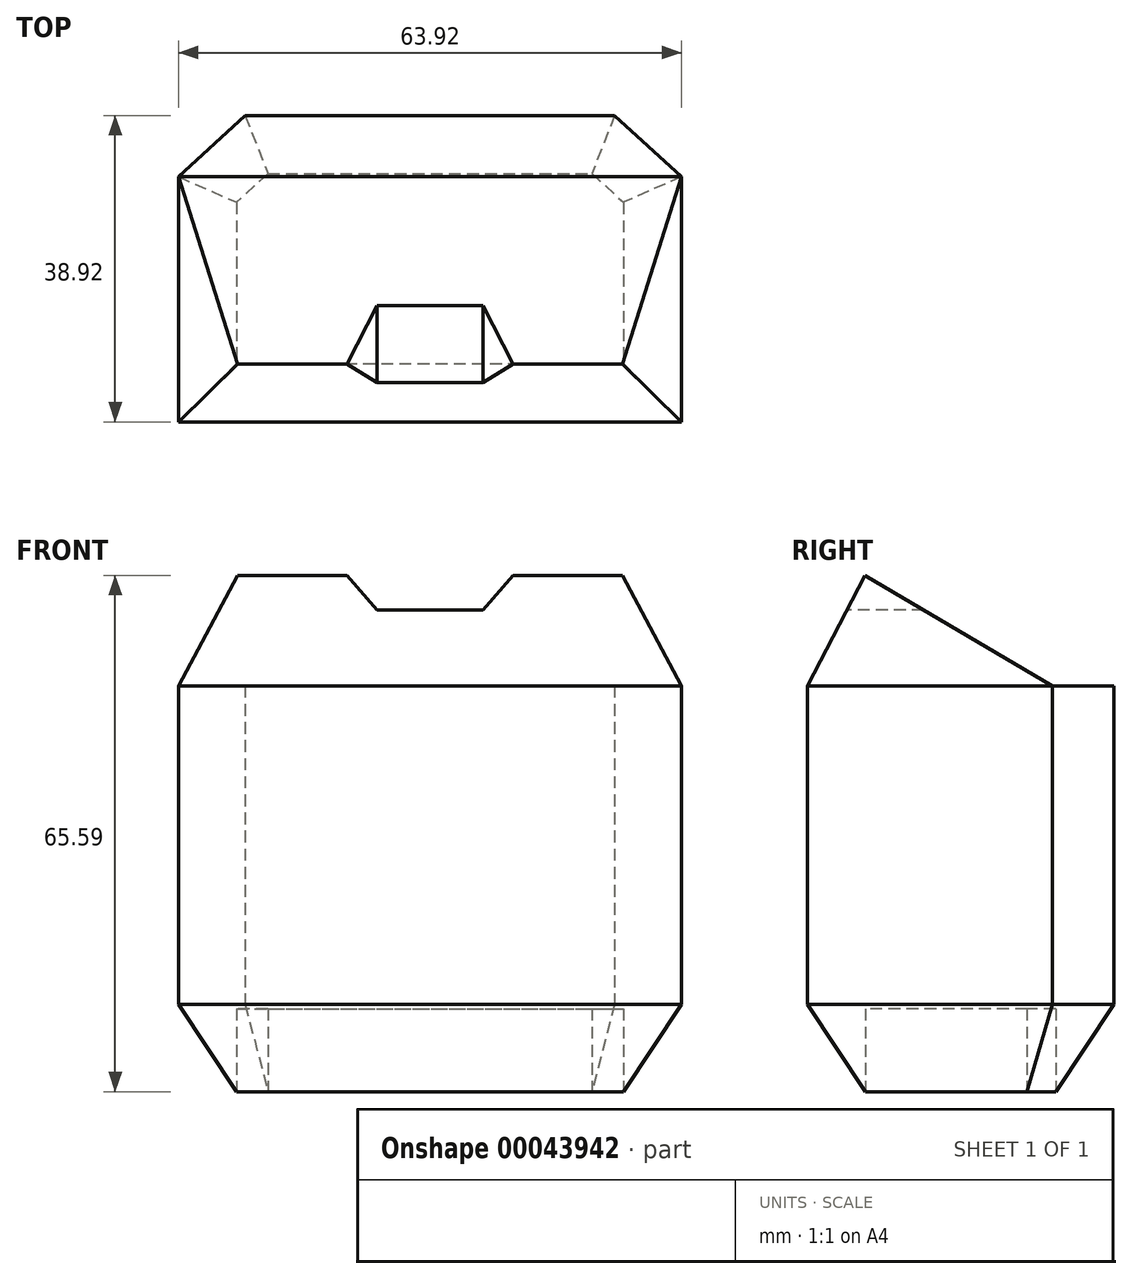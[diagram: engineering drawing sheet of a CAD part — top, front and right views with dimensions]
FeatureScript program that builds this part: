
annotation { "Feature Type Name" : "Feature", "Feature Type Description" : "" }
export const myFeature = defineFeature(function(context is Context, id is Id, definition is map)
    precondition{}
    {
        {
            var Q0;
            Q0=qCreatedBy(makeId("Top.planeOp"),FACE);
            var sketch = newSketch(context, id + "F0", { "sketchPlane" : qUnion([Q0])});
            skLineSegment(sketch, "E0", {"start": v(-23.46, 21.92) * mm, "end": v(23.46, 21.92) * mm});
            skLineSegment(sketch, "E1", {"start": v(23.46, 21.92) * mm, "end": v(31.96, 14.14) * mm});
            skLineSegment(sketch, "E2", {"start": v(31.96, 14.14) * mm, "end": v(31.96, -17) * mm});
            skLineSegment(sketch, "E3", {"start": v(31.96, -17) * mm, "end": v(0, -17) * mm});
            skLineSegment(sketch, "E4.MirrorCS", {"start": v(-31.96, 14.14) * mm, "end": v(-31.96, -17) * mm});
            skLineSegment(sketch, "E5.MirrorCS", {"start": v(-23.46, 21.92) * mm, "end": v(-31.96, 14.14) * mm});
            skLineSegment(sketch, "E6.MirrorCS", {"start": v(-31.96, -17) * mm, "end": v(0, -17) * mm});
            skLineSegment(sketch, "E7.0", {"start": v(-20.59, 14.54) * mm, "end": v(-24.57, 10.88) * mm});
            skLineSegment(sketch, "E7.1", {"start": v(-20.59, 14.54) * mm, "end": v(20.59, 14.54) * mm});
            skLineSegment(sketch, "E7.2", {"start": v(-24.57, -9.61) * mm, "end": v(0, -9.61) * mm});
            skLineSegment(sketch, "E7.3", {"start": v(24.57, -9.61) * mm, "end": v(0, -9.61) * mm});
            skLineSegment(sketch, "E7.4", {"start": v(24.57, 10.88) * mm, "end": v(24.57, -9.61) * mm});
            skLineSegment(sketch, "E7.5", {"start": v(-24.57, 10.88) * mm, "end": v(-24.57, -9.61) * mm});
            skLineSegment(sketch, "E7.6", {"start": v(20.59, 14.54) * mm, "end": v(24.57, 10.88) * mm});
            skSolve(sketch);
        }
        {
            var Q0;
            Q0=makeQuery(id+"F0.imprint","IMPRINT",FACE,{"disambiguationData":[TD([[makeQuery(id+"F0.imprint","IMPRINT",EDGE,{"derivedFrom":sQuery(id+"F0.wireOp",EDGE,"E7.0")}),1.0]])]});
            extrude(context, id + "F1", {"entities" : qUnion([Q0]), "depth" : 10.54 * mm});
        }
        {
            var Q0;
            Q0=makeQuery(id+"F1.opExtrude","SWEPT_BODY",BODY,{"disambiguationData":[OSD([sQuery(id+"F0.wireOp",EDGE,"E7.0"),sQuery(id+"F0.wireOp",EDGE,"E7.1"),sQuery(id+"F0.wireOp",EDGE,"E7.2"),sQuery(id+"F0.wireOp",EDGE,"E7.3"),sQuery(id+"F0.wireOp",EDGE,"E7.4"),sQuery(id+"F0.wireOp",EDGE,"E7.5"),sQuery(id+"F0.wireOp",EDGE,"E7.6")])]});
            var Q1;
            Q1=qCreatedBy(makeId("Top.planeOp"),FACE);
            transform(context, id + "F2", {"entities" : qUnion([Q0]), "transformType" : TransformType.TRANSLATION_DISTANCE, "transformDirection" : qUnion([Q1]), "distance" : 11.08 * mm, "oppositeDirection" : true, "makeCopy" : false});
        }
        {
            var Q0;
            Q0 = qSketchRegion(id + "F0", true);
            var Q1;
            Q1=makeQuery(id+"F0.imprint","IMPRINT",FACE,{"disambiguationData":[TD([[makeQuery(id+"F0.imprint","IMPRINT",EDGE,{"derivedFrom":sQuery(id+"F0.wireOp",EDGE,"E7.0")}),1.0]])]});
            extrude(context, id + "F3", {"entities" : qUnion([Q0, Q1]), "depth" : 40.48 * mm});
        }
        {
            var Q0;
            Q0=makeQuery(id+"F3.opExtrude","CAP_FACE",FACE,{"disambiguationData":[OSD([sQuery(id+"F0.wireOp",EDGE,"E0"),sQuery(id+"F0.wireOp",EDGE,"E1"),sQuery(id+"F0.wireOp",EDGE,"E2"),sQuery(id+"F0.wireOp",EDGE,"E3"),sQuery(id+"F0.wireOp",EDGE,"E4.MirrorCS"),sQuery(id+"F0.wireOp",EDGE,"E5.MirrorCS"),sQuery(id+"F0.wireOp",EDGE,"E6.MirrorCS")])],"isStart":true});
            var Q1;
            Q1=makeQuery(id+"F1.opExtrude","CAP_FACE",FACE,{"disambiguationData":[OSD([sQuery(id+"F0.wireOp",EDGE,"E7.0"),sQuery(id+"F0.wireOp",EDGE,"E7.1"),sQuery(id+"F0.wireOp",EDGE,"E7.2"),sQuery(id+"F0.wireOp",EDGE,"E7.3"),sQuery(id+"F0.wireOp",EDGE,"E7.4"),sQuery(id+"F0.wireOp",EDGE,"E7.5"),sQuery(id+"F0.wireOp",EDGE,"E7.6")])],"isStart":true});
            loft(context, id + "F4", {"sheetProfilesArray" : [{ "sheetProfileEntities" : qUnion([Q0]) }, { "sheetProfileEntities" : qUnion([Q1]) }]});
        }
        {
            var Q0;
            Q0=makeQuery(id+"F3.opExtrude","SWEPT_FACE",FACE,{"disambiguationData":[OSD([sQuery(id+"F0.wireOp",EDGE,"E4.MirrorCS")])]});
            var sketch = newSketch(context, id + "F5", { "sketchPlane" : qUnion([Q0])});
            skLineSegment(sketch, "E8", {"start": v(17, 40.48) * mm, "end": v(9.68, 54.5) * mm});
            skLineSegment(sketch, "E9", {"start": v(9.68, 54.5) * mm, "end": v(-14.14, 40.48) * mm});
            skSolve(sketch);
        }
        {
            var Q0;
            Q0=makeQuery(id+"F5.imprint","IMPRINT",FACE,{"disambiguationData":[TD([[makeQuery(id+"F5.imprint","IMPRINT",EDGE,{"derivedFrom":sQuery(id+"F5.wireOp",EDGE,"E8")}),1.0]])]});
            var Q1;
            Q1=makeQuery(id+"F3.opExtrude","SWEPT_FACE",FACE,{"disambiguationData":[OSD([sQuery(id+"F0.wireOp",EDGE,"E2")])]});
            extrude(context, id + "F6", {"entities" : qUnion([Q0]), "endBound" : BoundingType.UP_TO_SURFACE, "oppositeDirection" : true, "endBoundEntityFace" : qUnion([Q1]), "depth" : 25.4 * mm});
        }
        {
            var Q0;
            Q0=makeQuery(id+"F3.opExtrude","SWEPT_FACE",FACE,{"disambiguationData":[OSD([sQuery(id+"F0.wireOp",EDGE,"E3"),sQuery(id+"F0.wireOp",EDGE,"E6.MirrorCS")])]});
            var sketch = newSketch(context, id + "F7", { "sketchPlane" : qUnion([Q0])});
            skLineSegment(sketch, "E10.0", {"start": v(31.96, 54.5) * mm, "end": v(-31.96, 54.5) * mm});
            skLineSegment(sketch, "E11.0", {"start": v(-31.96, 40.48) * mm, "end": v(-31.96, 54.5) * mm});
            skLineSegment(sketch, "E12", {"start": v(-24.43, 54.5) * mm, "end": v(-10.53, 54.5) * mm});
            skLineSegment(sketch, "E13", {"start": v(-10.53, 54.5) * mm, "end": v(-6.73, 50.1) * mm});
            skLineSegment(sketch, "E14", {"start": v(-6.73, 50.1) * mm, "end": v(0, 50.1) * mm});
            skLineSegment(sketch, "E15.MirrorCS", {"start": v(24.43, 54.5) * mm, "end": v(10.53, 54.5) * mm});
            skLineSegment(sketch, "E16.MirrorCS", {"start": v(6.73, 50.1) * mm, "end": v(0, 50.1) * mm});
            skLineSegment(sketch, "E17.MirrorCS", {"start": v(10.53, 54.5) * mm, "end": v(6.73, 50.1) * mm});
            skLineSegment(sketch, "E18", {"start": v(-24.43, 54.5) * mm, "end": v(-31.96, 40.48) * mm});
            skLineSegment(sketch, "E19", {"start": v(24.43, 54.5) * mm, "end": v(31.96, 40.48) * mm});
            skLineSegment(sketch, "E20", {"start": v(31.96, 40.48) * mm, "end": v(31.96, 54.5) * mm});
            skSolve(sketch);
        }
        {
            var Q0;
            Q0 = qSketchRegion(id + "F7", true);
            extrude(context, id + "F8", {"entities" : qUnion([Q0]), "operationType" : NewBodyOperationType.REMOVE, "endBound" : BoundingType.THROUGH_ALL, "oppositeDirection" : true, "depth" : 25.4 * mm});
        }
    });
